# Revit family: DPD (2000-25000 cfm)
name_source: partatom
category: Mechanical Equipment
revit_build: Autodesk Revit 2015 (Build: 20140606_1530(x64)
units: mm (PartAtom-declared; Revit-internal decimal feet)

## types (11) — shared parameters
Description = Drop Diffuser / Plenums
Keynote = 2000-25000 cfm models
Manufacturer = United Enertech Corporation
Model = DPD
Type Comments = Size Options are Listed as Family Types
URL = https://unitedenertech.com

## per-type parameters (varying)
| type | B | F | Grille Height | Grille Length | T |
| DPD7215-62.5 (25000 cfm) | 6' - 10" | 1' - 6" | 1' - 3" | 6' - 0" | 4' - 4" |
| DPD7012-50 (20000 cfm) | 6' - 8" | 1' - 3" | 1' - 0" | 5' - 10" | 4' - 0" |
| DPD6012-40 (16000 cfm) | 5' - 10" | 1' - 3" | 1' - 0" | 5' - 0" | 3' - 4" |
| DPD5010-30 (12000 cfm) | 5' - 0" | 1' - 1" | 0' - 10" | 4' - 2" | 3' - 2" |
| DPD4010-25 (10000 cfm) | 4' - 2" | 1' - 1" | 0' - 10" | 3' - 4" | 3' - 0" |
| DPD3510-20 (8000 cfm) | 3' - 9" | 1' - 1" | 0' - 10" | 2' - 11" | 2' - 6" |
| DPD2510-15 (6000 cfm) | 2' - 11" | 1' - 1" | 0' - 10" | 2' - 1" | 2' - 4" |
| DPD2010-12.5 (5000 cfm) | 2' - 6" | 1' - 1" | 0' - 10" | 1' - 8" | 2' - 0" |
| DPD3006-10 (4000 cfm) | 3' - 4" | 0' - 9" | 0' - 6" | 2' - 6" | 1' - 10" |
| DPD1806-7.5 (3000 cfm) | 2' - 4" | 0' - 9" | 0' - 6" | 1' - 6" | 1' - 8" |
| DPD1206-5 (2000 cfm) | 1' - 10" | 0' - 9" | 0' - 6" | 1' - 0" | 1' - 2" |

## geometry (parser evidence)
native form markers: Sweep x7
no freeform markers — native parametric forms only
